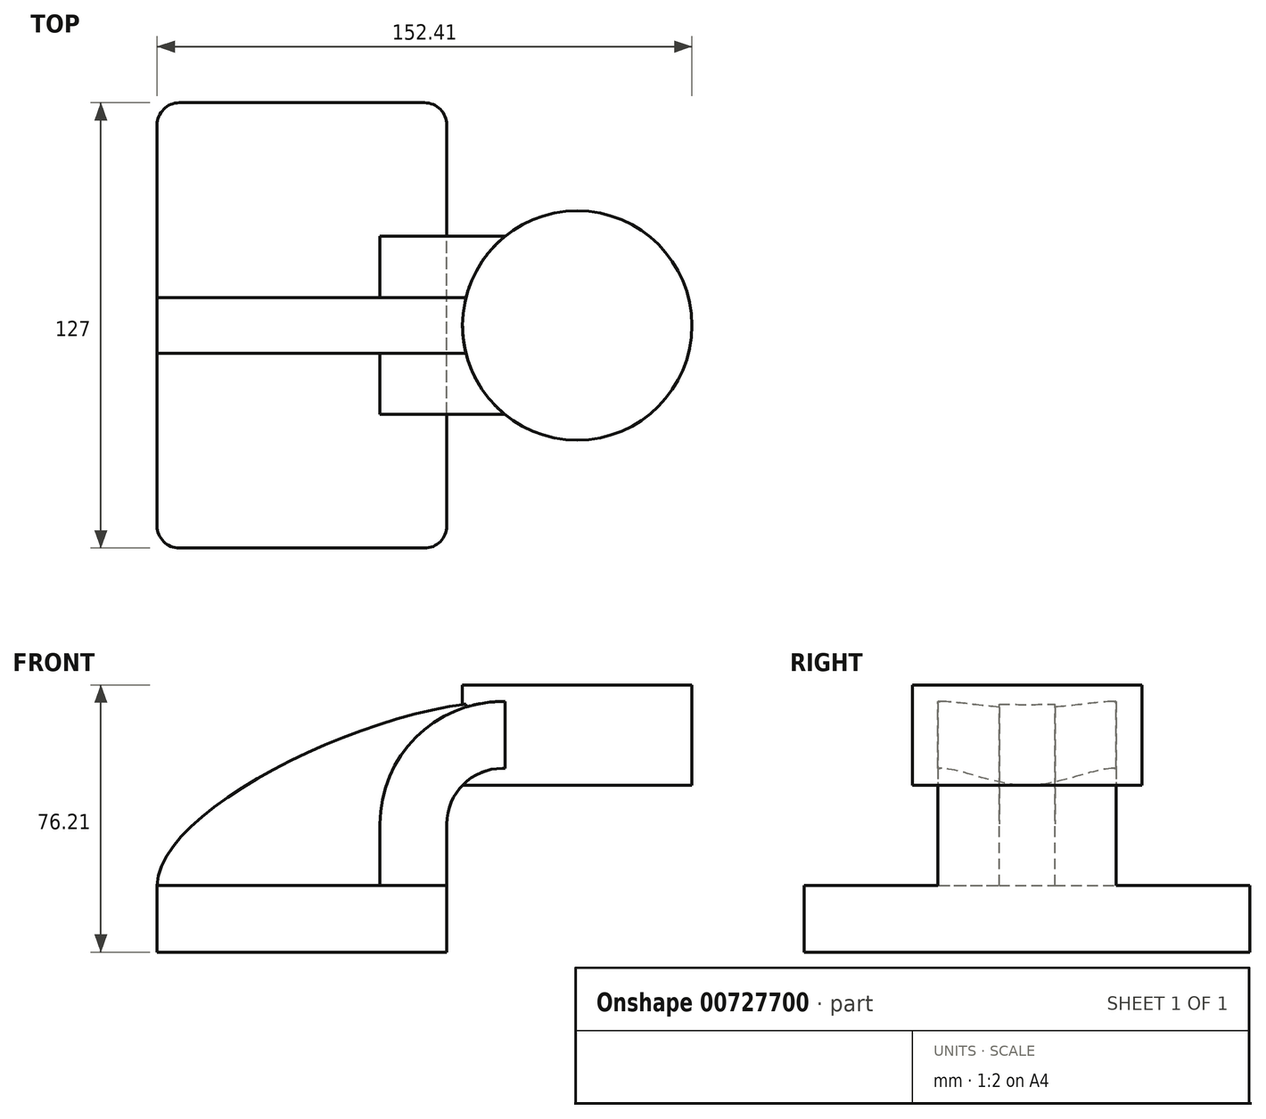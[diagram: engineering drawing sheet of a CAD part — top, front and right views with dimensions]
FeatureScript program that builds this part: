
annotation { "Feature Type Name" : "Feature", "Feature Type Description" : "" }
export const myFeature = defineFeature(function(context is Context, id is Id, definition is map)
    precondition{}
    {
        {
            var Q0;
            Q0=qCreatedBy(makeId("Front.planeOp"),FACE);
            var sketch = newSketch(context, id + "F0", { "sketchPlane" : qUnion([Q0])});
            skLineSegment(sketch, "E0.bottom", {"start": v(41.28, -9.52) * mm, "end": v(-41.28, -9.53) * mm});
            skLineSegment(sketch, "E0.top", {"start": v(41.28, 9.53) * mm, "end": v(-41.28, 9.53) * mm});
            skLineSegment(sketch, "E0.left", {"start": v(41.28, -9.52) * mm, "end": v(41.28, 9.53) * mm});
            skLineSegment(sketch, "E0.right", {"start": v(-41.28, -9.53) * mm, "end": v(-41.28, 9.53) * mm});
            skPoint(sketch, "E0.middle", {"position": v(0, 0) * mm});
            skLineSegment(sketch, "E1.bottom", {"start": v(111.12, 38.1) * mm, "end": v(60.32, 38.1) * mm});
            skLineSegment(sketch, "E1.top", {"start": v(111.12, 66.68) * mm, "end": v(60.32, 66.68) * mm});
            skLineSegment(sketch, "E1.left", {"start": v(111.12, 38.1) * mm, "end": v(111.12, 66.68) * mm});
            skLineSegment(sketch, "E1.right", {"start": v(60.32, 38.1) * mm, "end": v(60.32, 66.68) * mm});
            skPoint(sketch, "E1.middle", {"position": v(85.72, 52.39) * mm});
            skLineSegment(sketch, "E2", {"start": v(41.28, 9.53) * mm, "end": v(41.28, 27) * mm});
            skArc(sketch, "E3", {"start": v(41.27, 27) * mm, "mid": v(45.92, 38.23) * mm, "end": v(57.15, 42.88) * mm});
            skLineSegment(sketch, "E4", {"start": v(57.15, 42.88) * mm, "end": v(78.44, 42.88) * mm});
            skLineSegment(sketch, "E5.0", {"start": v(57.15, 61.93) * mm, "end": v(78.44, 61.93) * mm});
            skArc(sketch, "E5.1", {"start": v(22.23, 27) * mm, "mid": v(32.45, 51.7) * mm, "end": v(57.15, 61.93) * mm});
            skLineSegment(sketch, "E5.2", {"start": v(22.22, 9.53) * mm, "end": v(22.22, 27) * mm});
            skLineSegment(sketch, "E6", {"start": v(78.44, 61.93) * mm, "end": v(78.44, 42.88) * mm});
            skLineSegment(sketch, "E7", {"start": v(22.22, 9.53) * mm, "end": v(41.28, 9.53) * mm});
            skLineSegment(sketch, "E8", {"start": v(78.44, 61.93) * mm, "end": v(78.44, 66.68) * mm});
            skLineSegment(sketch, "E9", {"start": v(78.44, 66.68) * mm, "end": v(78.44, 38.1) * mm});
            skFitSpline(sketch, "E10", {"points": [v(-41.28, 9.52) * mm, v(57.15, 61.93) * mm], "startDerivative": vector(0.92, 67.53) * mm, "endDerivative": vector(103.2, -0.67) * mm});
            skSolve(sketch);
        }
        {
            var Q0;
            Q0=makeQuery(id+"F0.imprint","IMPRINT",FACE,{"disambiguationData":[TD([[makeQuery(id+"F0.imprint","IMPRINT",EDGE,{"derivedFrom":sQuery(id+"F0.wireOp",EDGE,"E0.bottom")}),-1.0]])]});
            extrude(context, id + "F1", {"entities" : qUnion([Q0]), "endBound" : BoundingType.SYMMETRIC, "depth" : 127 * mm, "offsetDistance" : 25.4 * mm});
        }
        {
            var Q0;
            Q0=makeQuery(id+"F0.imprint","IMPRINT",FACE,{"disambiguationData":[TD([[makeQuery(id+"F0.imprint","IMPRINT",EDGE,{"derivedFrom":sQuery(id+"F0.wireOp",EDGE,"E2")}),1.0]])]});
            var Q1;
            {var subQ0=sQuery(id+"F0.wireOp",EDGE,"E4");var subQ1=sQuery(id+"F0.wireOp",EDGE,"E1.right");var subQ2=makeQuery(id+"F0.imprint","INTERSECT",VERTEX,{"derivedFrom":[subQ1,subQ0]});Q1=makeQuery(id+"F0.imprint","IMPRINT",FACE,{"disambiguationData":[TD([[makeQuery(id+"F0.imprint","IMPRINT",EDGE,{"disambiguationData":[TD([[subQ2,-1.0]])],"derivedFrom":subQ1}),-1.0]])]});}
            extrude(context, id + "F2", {"entities" : qUnion([Q0, Q1]), "operationType" : NewBodyOperationType.ADD, "endBound" : BoundingType.SYMMETRIC, "depth" : 50.8 * mm, "offsetDistance" : 25.4 * mm});
        }
        {
            var Q0;
            Q0=makeQuery(id+"F0.imprint","IMPRINT",FACE,{"disambiguationData":[TD([[makeQuery(id+"F0.imprint","IMPRINT",EDGE,{"derivedFrom":sQuery(id+"F0.wireOp",EDGE,"E0.top")}),-1.0]])]});
            extrude(context, id + "F3", {"entities" : qUnion([Q0]), "operationType" : NewBodyOperationType.ADD, "endBound" : BoundingType.SYMMETRIC, "depth" : 15.88 * mm, "offsetDistance" : 25.4 * mm});
        }
        {
            var Q0;
            {var subQ0=sQuery(id+"F0.wireOp",EDGE,"E1.left");Q0=makeQuery(id+"F0.imprint","IMPRINT",FACE,{"disambiguationData":[TD([[makeQuery(id+"F0.imprint","IMPRINT",EDGE,{"derivedFrom":subQ0}),1.0]])]});}
            var Q1;
            Q1=sQuery(id+"F0.wireOp",EDGE,"E6");
            revolve(context, id + "F4", {"operationType" : NewBodyOperationType.ADD, "surfaceOperationType" : NewSurfaceOperationType.NEW, "entities" : qUnion([Q0]), "axis" : qUnion([Q1]), "revolveType" : RevolveType.FULL});
        }
        {
            var Q0;
            Q0=makeQuery(id+"F1.opExtrude","CAP_EDGE",EDGE,{"disambiguationData":[OSD([sQuery(id+"F0.wireOp",EDGE,"E0.left")])],"isStart":false});
            var Q1;
            Q1=makeQuery(id+"F1.opExtrude","CAP_EDGE",EDGE,{"disambiguationData":[OSD([sQuery(id+"F0.wireOp",EDGE,"E0.right")])],"isStart":false});
            var Q2;
            Q2=makeQuery(id+"F1.opExtrude","CAP_EDGE",EDGE,{"disambiguationData":[OSD([sQuery(id+"F0.wireOp",EDGE,"E0.left")])],"isStart":true});
            var Q3;
            Q3=makeQuery(id+"F1.opExtrude","CAP_EDGE",EDGE,{"disambiguationData":[OSD([sQuery(id+"F0.wireOp",EDGE,"E0.right")])],"isStart":true});
            fillet(context, id + "F5", {"entities" : qUnion([Q0, Q1, Q2, Q3]), "radius" : 6.35 * mm, "tangentPropagation" : true, "allowEdgeOverflow" : false});
        }
    });
